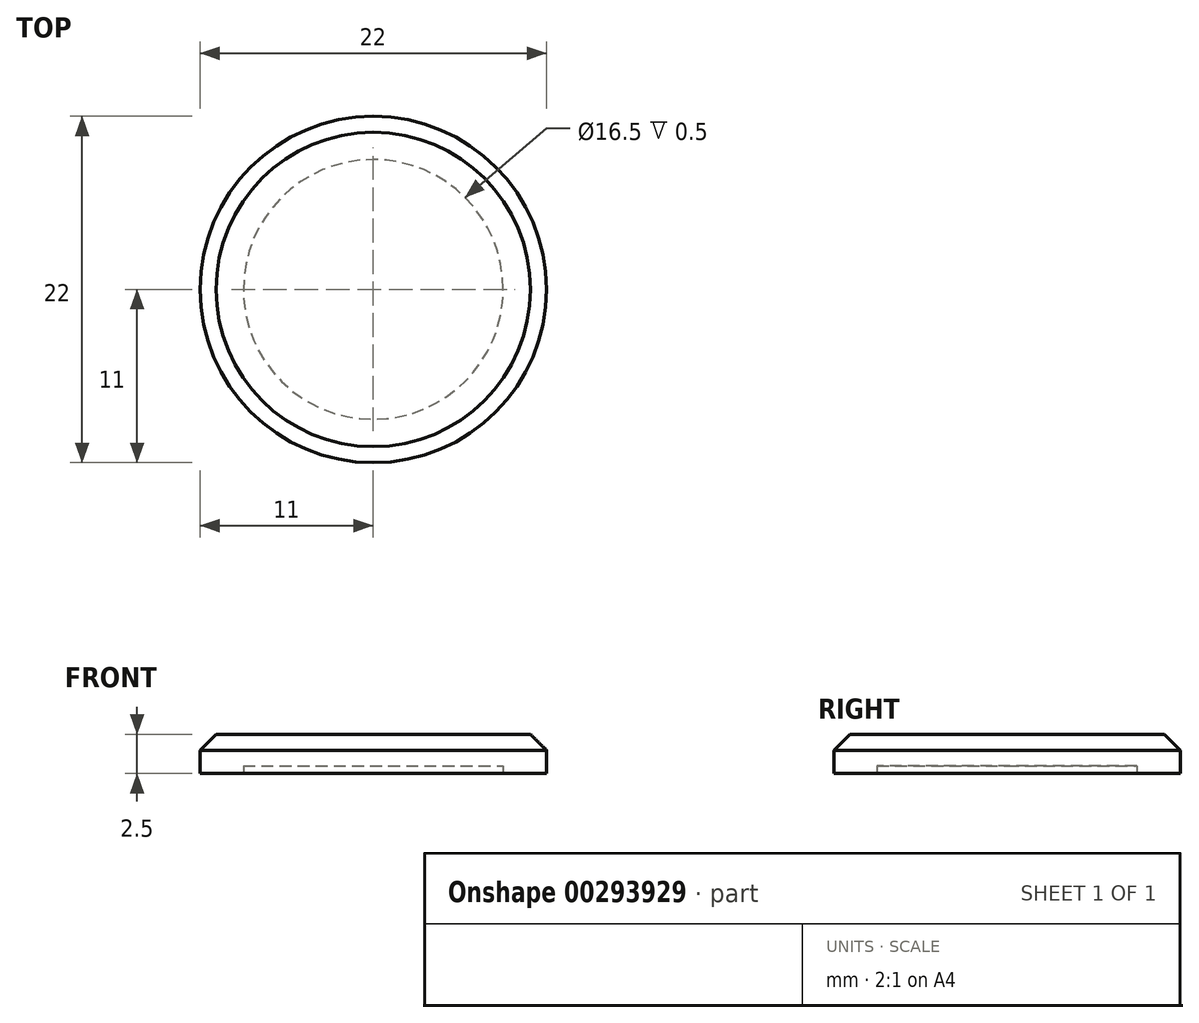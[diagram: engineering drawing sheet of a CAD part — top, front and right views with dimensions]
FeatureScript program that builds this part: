
annotation { "Feature Type Name" : "Feature", "Feature Type Description" : "" }
export const myFeature = defineFeature(function(context is Context, id is Id, definition is map)
    precondition{}
    {
        {
            var Q0;
            Q0=qCreatedBy(makeId("Top.planeOp"),FACE);
            var sketch = newSketch(context, id + "F0", { "sketchPlane" : qUnion([Q0])});
            skCircle(sketch, "E0", {"center": v(0, 0) * mm, "radius": 11 * mm});
            skSolve(sketch);
        }
        {
            var Q0;
            Q0=qSketchRegion(id+"F0",true);
            extrude(context, id + "F1", {"entities" : qUnion([Q0]), "depth" : 2.5 * mm});
        }
        {
            var Q0;
            Q0=makeQuery(id+"F1.opExtrude","CAP_EDGE",EDGE,{"disambiguationData":[OSD([sQuery(id+"F0.wireOp",EDGE,"E0")])],"isStart":false});
            chamfer(context, id + "F2", {"entities" : qUnion([Q0]), "width" : 1.02 * mm, "tangentPropagation" : true});
        }
        {
            var Q0;
            Q0=makeQuery(id+"F1.opExtrude","CAP_FACE",FACE,{"disambiguationData":[OSD([sQuery(id+"F0.wireOp",EDGE,"E0")])],"isStart":true});
            var sketch = newSketch(context, id + "F3", { "sketchPlane" : qUnion([Q0])});
            skCircle(sketch, "E1", {"center": v(0, 0) * mm, "radius": 8.25 * mm});
            skSolve(sketch);
        }
        {
            var Q0;
            Q0=qSketchRegion(id+"F3",true);
            extrude(context, id + "F4", {"entities" : qUnion([Q0]), "operationType" : NewBodyOperationType.REMOVE, "oppositeDirection" : true, "depth" : .5 * mm});
        }
    });
